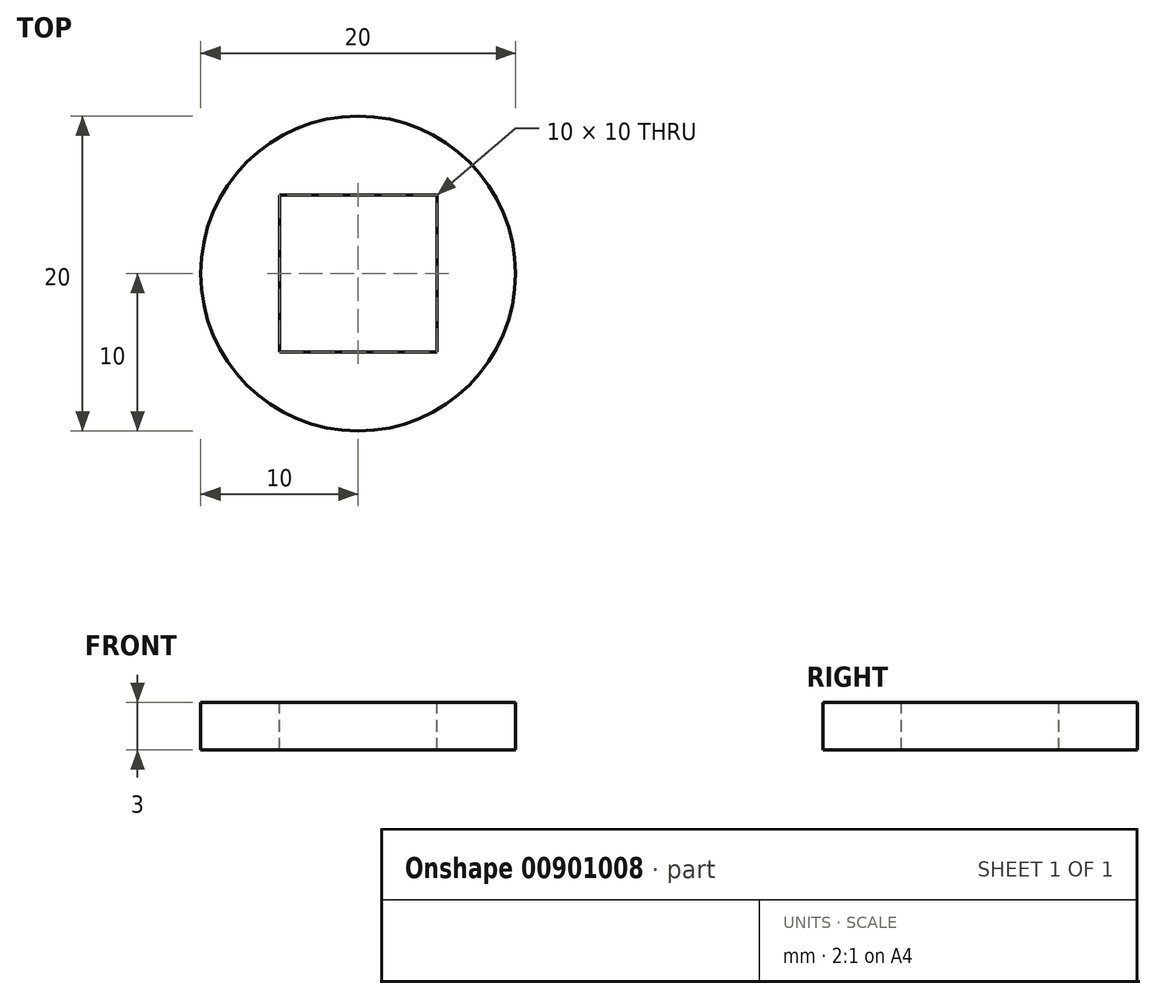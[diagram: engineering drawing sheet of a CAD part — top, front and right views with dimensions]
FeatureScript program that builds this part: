
annotation { "Feature Type Name" : "Feature", "Feature Type Description" : "" }
export const myFeature = defineFeature(function(context is Context, id is Id, definition is map)
    precondition{}
    {
        {
            var Q0;
            Q0=qCreatedBy(makeId("Top.planeOp"),FACE);
            var sketch = newSketch(context, id + "F0", { "sketchPlane" : qUnion([Q0])});
            skCircle(sketch, "E0", {"center": v(0, 0) * mm, "radius": 10 * mm});
            skSolve(sketch);
        }
        {
            var Q0;
            Q0 = qSketchRegion(id + "F0", true);
            extrude(context, id + "F1", {"entities" : qUnion([Q0]), "depth" : 3 * mm, "offsetDistance" : 25 * mm});
        }
        {
            var Q0;
            Q0=makeQuery(id+"F1.opExtrude","CAP_FACE",FACE,{"disambiguationData":[OSD([sQuery(id+"F0.wireOp",EDGE,"E0")])],"isStart":false});
            var sketch = newSketch(context, id + "F2", { "sketchPlane" : qUnion([Q0])});
            skLineSegment(sketch, "E1.bottom", {"start": v(5, -5) * mm, "end": v(-5, -5) * mm});
            skLineSegment(sketch, "E1.top", {"start": v(5, 5) * mm, "end": v(-5, 5) * mm});
            skLineSegment(sketch, "E1.left", {"start": v(5, -5) * mm, "end": v(5, 5) * mm});
            skLineSegment(sketch, "E1.right", {"start": v(-5, -5) * mm, "end": v(-5, 5) * mm});
            skPoint(sketch, "E1.middle", {"position": v(0, 0) * mm});
            skSolve(sketch);
        }
        {
            var Q0;
            Q0 = qSketchRegion(id + "F2", true);
            extrude(context, id + "F3", {"entities" : qUnion([Q0]), "operationType" : NewBodyOperationType.REMOVE, "endBound" : BoundingType.THROUGH_ALL, "oppositeDirection" : true, "depth" : 25 * mm, "offsetDistance" : 25 * mm});
        }
    });
